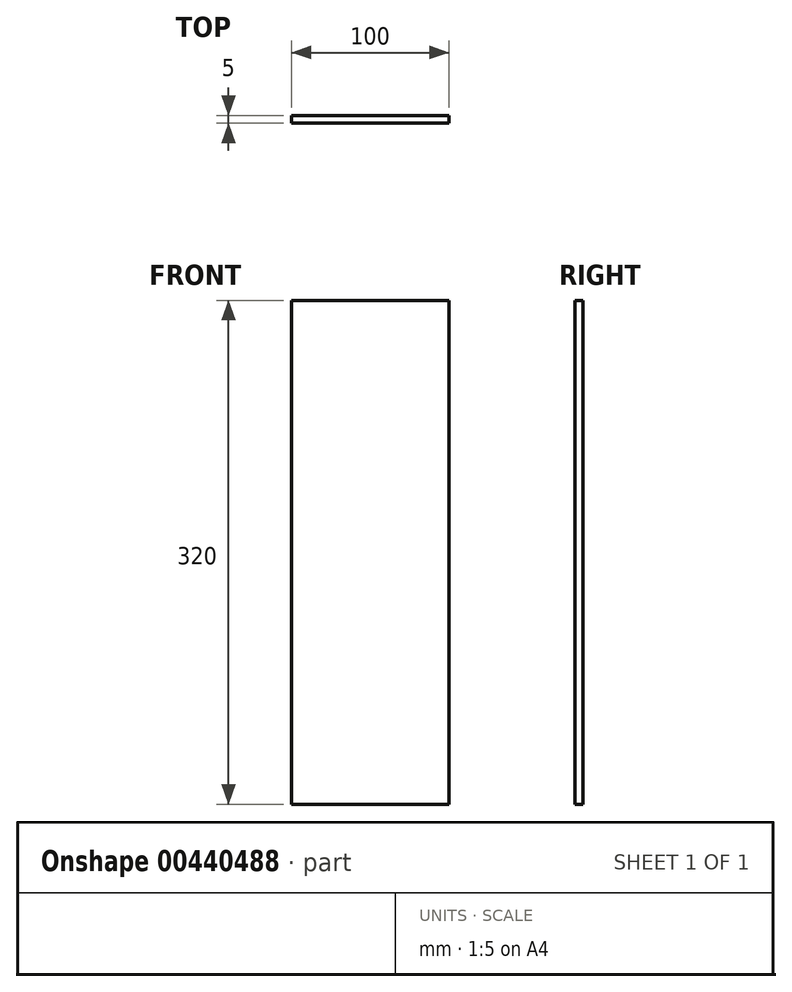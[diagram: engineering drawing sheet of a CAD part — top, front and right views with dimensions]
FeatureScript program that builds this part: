
annotation { "Feature Type Name" : "Feature", "Feature Type Description" : "" }
export const myFeature = defineFeature(function(context is Context, id is Id, definition is map)
    precondition{}
    {
        {
            var Q0;
            Q0=qCreatedBy(makeId("Front.planeOp"),FACE);
            var sketch = newSketch(context, id + "F0", { "sketchPlane" : qUnion([Q0])});
            skLineSegment(sketch, "E0.bottom", {"start": v(-50, 160) * mm, "end": v(50, 160) * mm});
            skLineSegment(sketch, "E0.top", {"start": v(-50, -160) * mm, "end": v(50, -160) * mm});
            skLineSegment(sketch, "E0.left", {"start": v(-50, 160) * mm, "end": v(-50, -160) * mm});
            skLineSegment(sketch, "E0.right", {"start": v(50, 160) * mm, "end": v(50, -160) * mm});
            skPoint(sketch, "E0.middle", {"position": v(0, 0) * mm});
            skSolve(sketch);
        }
        {
            var Q0;
            Q0 = qSketchRegion(id + "F0", true);
            extrude(context, id + "F1", {"entities" : qUnion([Q0]), "depth" : 5 * mm});
        }
    });
